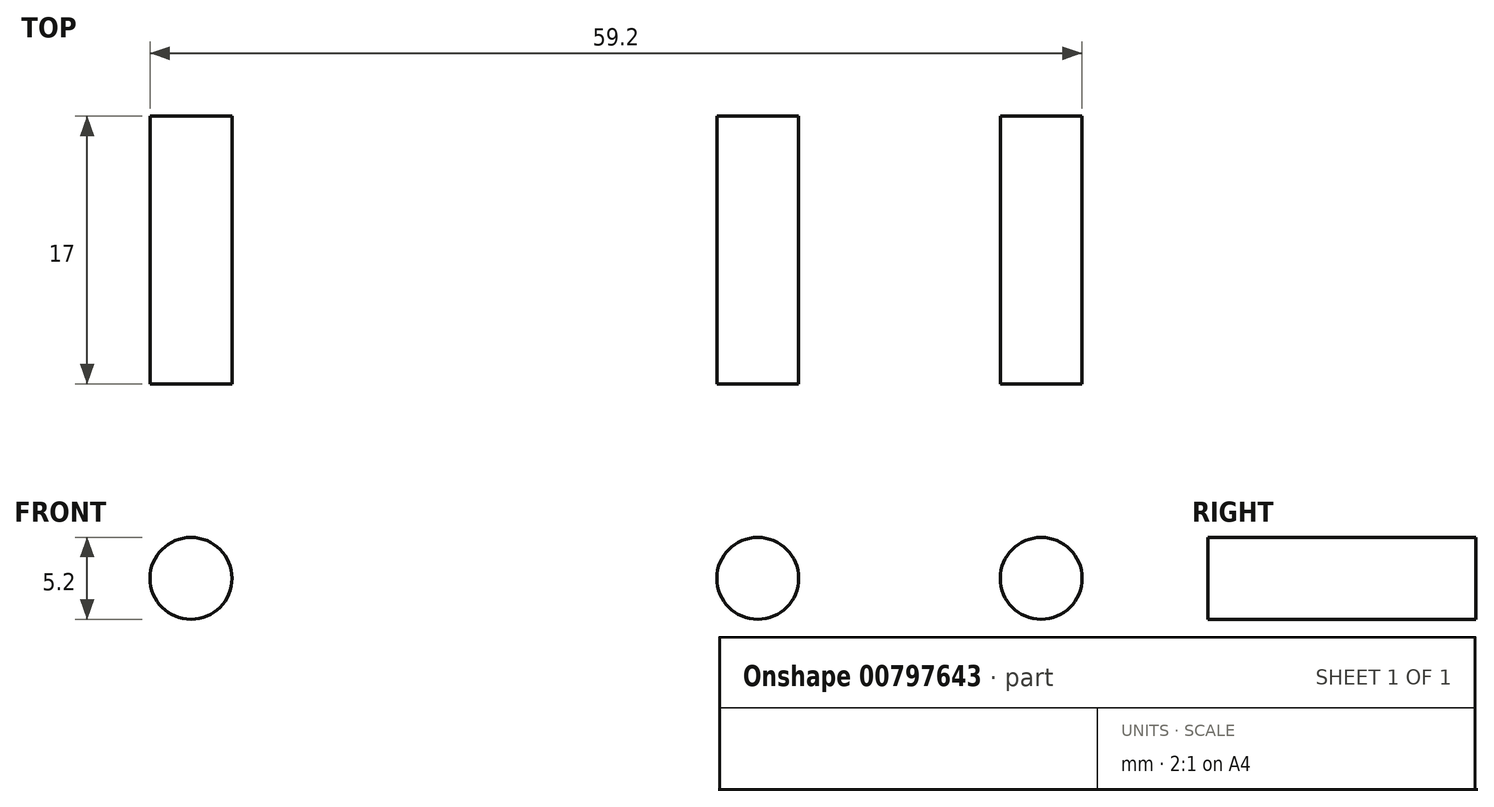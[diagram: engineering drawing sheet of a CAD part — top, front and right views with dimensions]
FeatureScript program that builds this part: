
annotation { "Feature Type Name" : "Feature", "Feature Type Description" : "" }
export const myFeature = defineFeature(function(context is Context, id is Id, definition is map)
    precondition{}
    {
        {
            var Q0;
            Q0=qCreatedBy(makeId("Top.planeOp"),FACE);
            var sketch = newSketch(context, id + "F0", { "sketchPlane" : qUnion([Q0])});
            skLineSegment(sketch, "E0.bottom", {"start": v(43, -8.5) * mm, "end": v(-43, -8.5) * mm});
            skLineSegment(sketch, "E0.top", {"start": v(43, 8.5) * mm, "end": v(-43, 8.5) * mm});
            skLineSegment(sketch, "E0.left", {"start": v(43, -8.5) * mm, "end": v(43, 8.5) * mm});
            skLineSegment(sketch, "E0.right", {"start": v(-43, -8.5) * mm, "end": v(-43, 8.5) * mm});
            skPoint(sketch, "E0.middle", {"position": v(0, 0) * mm});
            skLineSegment(sketch, "E1", {"start": v(0, 0) * mm, "end": v(-28, 0) * mm, "construction": true});
            skCircle(sketch, "E2", {"center": v(-28, 0) * mm, "radius": 2 * mm});
            skCircle(sketch, "E3.MirrorC", {"center": v(28, 0) * mm, "radius": 2 * mm});
            skSolve(sketch);
        }
        {
            var Q0;
            Q0 = qSketchRegion(id + "F0", true);
            extrude(context, id + "F1", {"entities" : qUnion([Q0]), "depth" : 15 * mm, "offsetDistance" : 25 * mm});
        }
        {
            var Q0;
            Q0=makeQuery(id+"F1.opExtrude","SWEPT_FACE",FACE,{"disambiguationData":[OSD([sQuery(id+"F0.wireOp",EDGE,"E0.bottom")])]});
            var sketch = newSketch(context, id + "F2", { "sketchPlane" : qUnion([Q0])});
            skLineSegment(sketch, "E4", {"start": v(0, 0) * mm, "end": v(0, -15.88) * mm, "construction": true});
            skLineSegment(sketch, "E5", {"start": v(-41.33, 0) * mm, "end": v(-41.33, 9) * mm, "construction": true});
            skLineSegment(sketch, "E6", {"start": v(-41.33, 9) * mm, "end": v(62.94, 9) * mm, "construction": true});
            skLineSegment(sketch, "E7", {"start": v(-41.33, 9) * mm, "end": v(-75.28, 9) * mm, "construction": true});
            skLineSegment(sketch, "E8", {"start": v(0, -10.3) * mm, "end": v(-36, -10.3) * mm, "construction": true});
            skLineSegment(sketch, "E9", {"start": v(0, -4.53) * mm, "end": v(-18, -4.53) * mm, "construction": true});
            skLineSegment(sketch, "E10", {"start": v(-36, -10.3) * mm, "end": v(-36, 26.86) * mm, "construction": true});
            skLineSegment(sketch, "E11", {"start": v(-18, -4.53) * mm, "end": v(-18, 30.47) * mm});
            skCircle(sketch, "E12", {"center": v(0, 9) * mm, "radius": 2.6 * mm});
            skCircle(sketch, "E13", {"center": v(-18, 9) * mm, "radius": 2.6 * mm});
            skCircle(sketch, "E14", {"center": v(-36, 9) * mm, "radius": 2.6 * mm});
            skPoint(sketch, "E14.centerSnap0", {"position": v(-36, 8.28) * mm});
            skCircle(sketch, "E15.MirrorC", {"center": v(18, 9) * mm, "radius": 2.6 * mm});
            skCircle(sketch, "E16.MirrorC", {"center": v(36, 9) * mm, "radius": 2.6 * mm});
            skSolve(sketch);
        }
        {
            var Q0;
            Q0=makeQuery(id+"F2.imprint","IMPRINT",FACE,{"disambiguationData":[TD([[makeQuery(id+"F2.imprint","IMPRINT",EDGE,{"derivedFrom":sQuery(id+"F2.wireOp",EDGE,"E14")}),1.0]])]});
            var Q1;
            {var subQ0=sQuery(id+"F2.wireOp",EDGE,"E13");var subQ1=sQuery(id+"F2.wireOp",EDGE,"E11");var subQ2=makeQuery(id+"F2.imprint","INTERSECT",VERTEX,{"disambiguationData":[OD(0.0)],"derivedFrom":[subQ1,subQ0]});Q1=makeQuery(id+"F2.imprint","IMPRINT",FACE,{"disambiguationData":[TD([[makeQuery(id+"F2.imprint","IMPRINT",EDGE,{"disambiguationData":[TD([[subQ2,-1.0]])],"derivedFrom":subQ1}),1.0]])]});}
            var Q2;
            {var subQ0=sQuery(id+"F2.wireOp",EDGE,"E13");var subQ1=sQuery(id+"F2.wireOp",EDGE,"E11");var subQ2=makeQuery(id+"F2.imprint","INTERSECT",VERTEX,{"disambiguationData":[OD(0.0)],"derivedFrom":[subQ1,subQ0]});Q2=makeQuery(id+"F2.imprint","IMPRINT",FACE,{"disambiguationData":[TD([[makeQuery(id+"F2.imprint","IMPRINT",EDGE,{"disambiguationData":[TD([[subQ2,-1.0]])],"derivedFrom":subQ1}),-1.0]])]});}
            var Q3;
            Q3=makeQuery(id+"F2.imprint","IMPRINT",FACE,{"disambiguationData":[TD([[makeQuery(id+"F2.imprint","IMPRINT",EDGE,{"derivedFrom":sQuery(id+"F2.wireOp",EDGE,"E12")}),1.0]])]});
            var Q4;
            Q4=makeQuery(id+"F2.imprint","IMPRINT",FACE,{"disambiguationData":[TD([[makeQuery(id+"F2.imprint","IMPRINT",EDGE,{"derivedFrom":sQuery(id+"F2.wireOp",EDGE,"E15.MirrorC")}),-1.0]])]});
            var Q5;
            Q5=makeQuery(id+"F2.imprint","IMPRINT",FACE,{"disambiguationData":[TD([[makeQuery(id+"F2.imprint","IMPRINT",EDGE,{"derivedFrom":sQuery(id+"F2.wireOp",EDGE,"E16.MirrorC")}),-1.0]])]});
            var Q6;
            Q6=sQuery(id+"F2.wireOp",EDGE,"E14");
            var Q7;
            Q7=sQuery(id+"F2.wireOp",EDGE,"E13");
            var Q8;
            Q8=sQuery(id+"F2.wireOp",EDGE,"E12");
            var Q9;
            Q9=sQuery(id+"F2.wireOp",EDGE,"E15.MirrorC");
            var Q10;
            Q10=sQuery(id+"F2.wireOp",EDGE,"E16.MirrorC");
            extrude(context, id + "F3", {"entities" : qUnion([Q0, Q1, Q2, Q3, Q4, Q5]), "operationType" : NewBodyOperationType.REMOVE, "surfaceEntities" : qUnion([Q6, Q7, Q8, Q9, Q10]), "endBound" : BoundingType.THROUGH_ALL, "oppositeDirection" : true, "depth" : 25 * mm, "offsetDistance" : 25 * mm});
        }
    });
